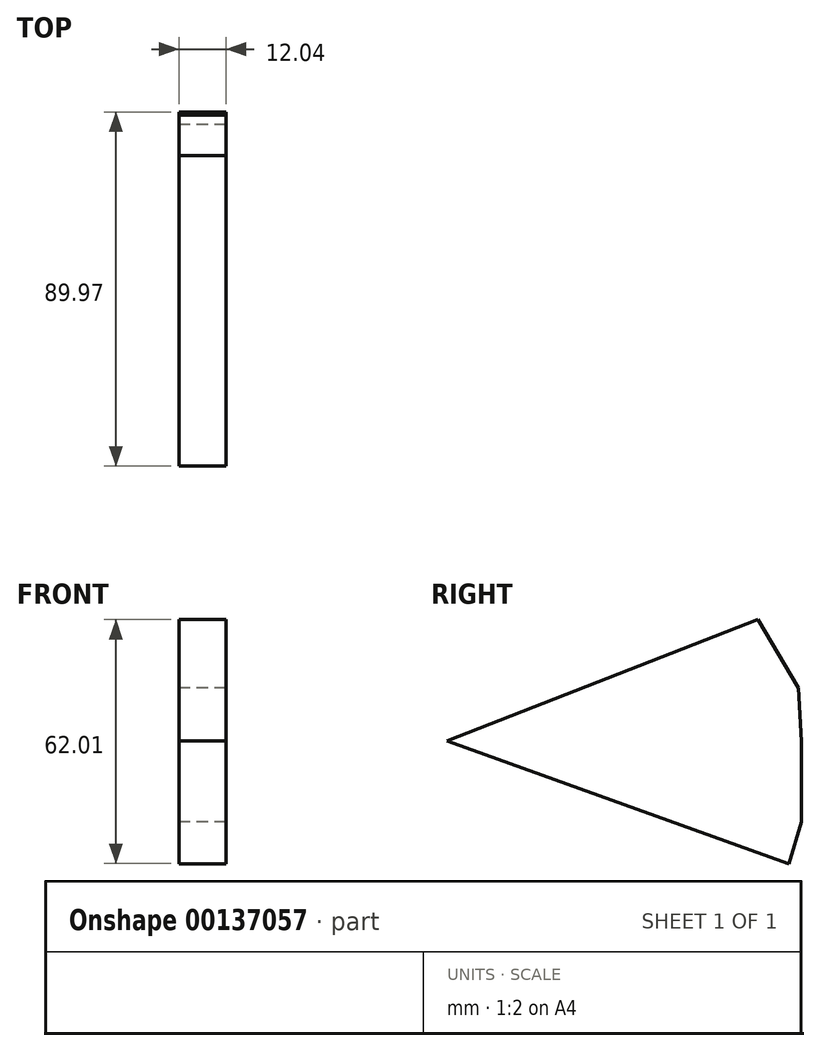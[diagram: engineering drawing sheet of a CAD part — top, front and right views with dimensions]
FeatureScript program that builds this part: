
annotation { "Feature Type Name" : "Feature", "Feature Type Description" : "" }
export const myFeature = defineFeature(function(context is Context, id is Id, definition is map)
    precondition{}
    {
        {
            var Q0;
            Q0=qCreatedBy(makeId("Right.planeOp"),FACE);
            var sketch = newSketch(context, id + "F0", { "sketchPlane" : qUnion([Q0])});
            skLineSegment(sketch, "E0", {"start": v(-29.7, 34.02) * mm, "end": v(-64.38, 28.77) * mm});
            skLineSegment(sketch, "E1", {"start": v(-64.38, 28.77) * mm, "end": v(-28.9, 20.36) * mm});
            skLineSegment(sketch, "E2", {"start": v(-28.9, 20.36) * mm, "end": v(-29.7, 34.02) * mm});
            skLineSegment(sketch, "E3", {"start": v(-28.9, 20.36) * mm, "end": v(-28.9, 0) * mm});
            skLineSegment(sketch, "E4", {"start": v(-28.9, 0) * mm, "end": v(-68.84, 17.47) * mm});
            skLineSegment(sketch, "E5", {"start": v(-68.84, 17.47) * mm, "end": v(-28.9, 17.47) * mm});
            skLineSegment(sketch, "E6", {"start": v(-28.9, 17.47) * mm, "end": v(-28.9, 20.36) * mm});
            skLineSegment(sketch, "E7", {"start": v(-64.38, 28.77) * mm, "end": v(-92.76, 24.47) * mm});
            skLineSegment(sketch, "E8", {"start": v(-92.76, 24.47) * mm, "end": v(-68.84, 17.47) * mm});
            skLineSegment(sketch, "E9", {"start": v(-92.76, 24.47) * mm, "end": v(-118.87, 20.51) * mm});
            skLineSegment(sketch, "E10", {"start": v(-118.87, 20.51) * mm, "end": v(-32.06, -10.64) * mm});
            skLineSegment(sketch, "E11", {"start": v(-32.06, -10.64) * mm, "end": v(-28.9, 0) * mm});
            skLineSegment(sketch, "E12", {"start": v(-118.87, 20.51) * mm, "end": v(-39.94, 51.37) * mm});
            skLineSegment(sketch, "E13", {"start": v(-39.94, 51.37) * mm, "end": v(-29.7, 34.02) * mm});
            skSolve(sketch);
        }
        {
            var Q0;
            Q0=makeQuery(id+"F0.imprint","IMPRINT",FACE,{"disambiguationData":[TD([[makeQuery(id+"F0.imprint","IMPRINT",EDGE,{"derivedFrom":sQuery(id+"F0.wireOp",EDGE,"E0")}),1.0]])]});
            var Q1;
            Q1=makeQuery(id+"F0.imprint","IMPRINT",FACE,{"disambiguationData":[TD([[makeQuery(id+"F0.imprint","IMPRINT",EDGE,{"derivedFrom":sQuery(id+"F0.wireOp",EDGE,"E0")}),-1.0]])]});
            var Q2;
            Q2=makeQuery(id+"F0.imprint","IMPRINT",FACE,{"disambiguationData":[TD([[makeQuery(id+"F0.imprint","IMPRINT",EDGE,{"derivedFrom":sQuery(id+"F0.wireOp",EDGE,"E3")}),-1.0]])]});
            var Q3;
            Q3=makeQuery(id+"F0.imprint","IMPRINT",FACE,{"disambiguationData":[TD([[makeQuery(id+"F0.imprint","IMPRINT",EDGE,{"derivedFrom":sQuery(id+"F0.wireOp",EDGE,"E1")}),-1.0]])]});
            var Q4;
            Q4=makeQuery(id+"F0.imprint","IMPRINT",FACE,{"disambiguationData":[TD([[makeQuery(id+"F0.imprint","IMPRINT",EDGE,{"derivedFrom":sQuery(id+"F0.wireOp",EDGE,"E4")}),1.0]])]});
            var Q5;
            Q5=sQuery(id+"F0.wireOp",EDGE,"E7");
            var Q6;
            Q6=sQuery(id+"F0.wireOp",EDGE,"E5");
            var Q7;
            Q7=sQuery(id+"F0.wireOp",EDGE,"E8");
            var Q8;
            Q8=sQuery(id+"F0.wireOp",EDGE,"E4");
            var Q9;
            Q9=sQuery(id+"F0.wireOp",EDGE,"E9");
            var Q10;
            Q10=sQuery(id+"F0.wireOp",EDGE,"E3");
            var Q11;
            Q11=sQuery(id+"F0.wireOp",EDGE,"E10");
            var Q12;
            Q12=sQuery(id+"F0.wireOp",EDGE,"E11");
            var Q13;
            Q13=sQuery(id+"F0.wireOp",EDGE,"E2");
            var Q14;
            Q14=sQuery(id+"F0.wireOp",EDGE,"E12");
            var Q15;
            Q15=sQuery(id+"F0.wireOp",EDGE,"E1");
            var Q16;
            Q16=sQuery(id+"F0.wireOp",EDGE,"E13");
            var Q17;
            Q17=sQuery(id+"F0.wireOp",EDGE,"E0");
            var Q18;
            Q18=sQuery(id+"F0.wireOp",EDGE,"E6");
            extrude(context, id + "F1", {"entities" : qUnion([Q0, Q1, Q2, Q3, Q4]), "surfaceEntities" : qUnion([Q5, Q6, Q7, Q8, Q9, Q10, Q11, Q12, Q13, Q14, Q15, Q16, Q17, Q18]), "depth" : 12.04 * mm});
        }
    });
